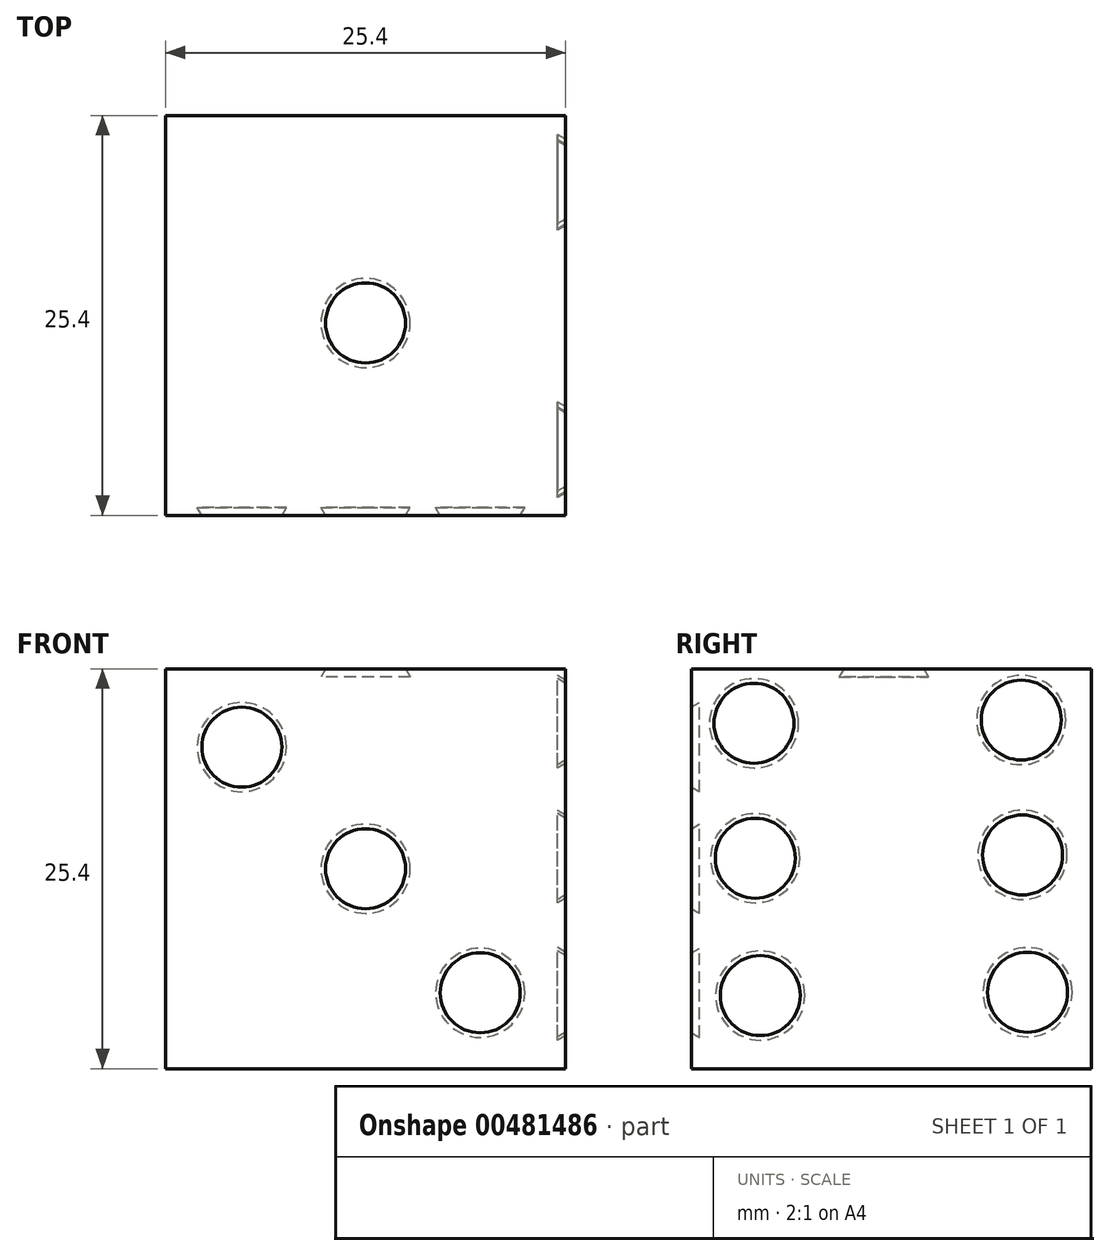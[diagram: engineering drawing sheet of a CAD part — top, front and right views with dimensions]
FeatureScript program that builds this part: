
annotation { "Feature Type Name" : "Feature", "Feature Type Description" : "" }
export const myFeature = defineFeature(function(context is Context, id is Id, definition is map)
    precondition{}
    {
        {
            var Q0;
            Q0=qCreatedBy(makeId("Front.planeOp"),FACE);
            var sketch = newSketch(context, id + "F0", { "sketchPlane" : qUnion([Q0])});
            skLineSegment(sketch, "E0.bottom", {"start": v(-12.7, 12.7) * mm, "end": v(12.7, 12.7) * mm});
            skLineSegment(sketch, "E0.top", {"start": v(-12.7, -12.7) * mm, "end": v(12.7, -12.7) * mm});
            skLineSegment(sketch, "E0.left", {"start": v(-12.7, 12.7) * mm, "end": v(-12.7, -12.7) * mm});
            skLineSegment(sketch, "E0.right", {"start": v(12.7, 12.7) * mm, "end": v(12.7, -12.7) * mm});
            skPoint(sketch, "E0.middle", {"position": v(0, 0) * mm});
            skSolve(sketch);
        }
        {
            var Q0;
            Q0=makeQuery(id+"F0.imprint","IMPRINT",FACE,{"disambiguationData":[TD([[makeQuery(id+"F0.imprint","IMPRINT",EDGE,{"derivedFrom":sQuery(id+"F0.wireOp",EDGE,"E0.bottom")}),-1.0]])]});
            extrude(context, id + "F1", {"entities" : qUnion([Q0]), "depth" : 25.4 * mm});
        }
        {
            var Q0;
            Q0=makeQuery(id+"F1.opExtrude","SWEPT_FACE",FACE,{"disambiguationData":[OSD([sQuery(id+"F0.wireOp",EDGE,"E0.bottom")])]});
            var sketch = newSketch(context, id + "F2", { "sketchPlane" : qUnion([Q0])});
            skCircle(sketch, "E1", {"center": v(0, -13.19) * mm, "radius": 2.54 * mm});
            skSolve(sketch);
        }
        {
            var Q0;
            Q0=makeQuery(id+"F2.imprint","IMPRINT",FACE,{"disambiguationData":[TD([[makeQuery(id+"F2.imprint","IMPRINT",EDGE,{"derivedFrom":sQuery(id+"F2.wireOp",EDGE,"E1")}),1.0]])]});
            extrude(context, id + "F3", {"entities" : qUnion([Q0]), "operationType" : NewBodyOperationType.REMOVE, "oppositeDirection" : true, "depth" : 0.5 * mm, "hasDraft" : true, "draftAngle" : 30 * degree});
        }
        {
            var Q0;
            Q0=makeQuery(id+"F1.opExtrude","CAP_FACE",FACE,{"disambiguationData":[OSD([sQuery(id+"F0.wireOp",EDGE,"E0.bottom"),sQuery(id+"F0.wireOp",EDGE,"E0.top"),sQuery(id+"F0.wireOp",EDGE,"E0.left"),sQuery(id+"F0.wireOp",EDGE,"E0.right")])],"isStart":false});
            var sketch = newSketch(context, id + "F4", { "sketchPlane" : qUnion([Q0])});
            skCircle(sketch, "E2", {"center": v(0, 0) * mm, "radius": 2.54 * mm});
            skCircle(sketch, "E3", {"center": v(7.28, -7.88) * mm, "radius": 2.54 * mm});
            skCircle(sketch, "E4", {"center": v(-7.86, 7.72) * mm, "radius": 2.54 * mm});
            skSolve(sketch);
        }
        {
            var Q0;
            Q0=makeQuery(id+"F4.imprint","IMPRINT",FACE,{"disambiguationData":[TD([[makeQuery(id+"F4.imprint","IMPRINT",EDGE,{"derivedFrom":sQuery(id+"F4.wireOp",EDGE,"E4")}),1.0]])]});
            var Q1;
            Q1=makeQuery(id+"F4.imprint","IMPRINT",FACE,{"disambiguationData":[TD([[makeQuery(id+"F4.imprint","IMPRINT",EDGE,{"derivedFrom":sQuery(id+"F4.wireOp",EDGE,"E2")}),1.0]])]});
            var Q2;
            Q2=makeQuery(id+"F4.imprint","IMPRINT",FACE,{"disambiguationData":[TD([[makeQuery(id+"F4.imprint","IMPRINT",EDGE,{"derivedFrom":sQuery(id+"F4.wireOp",EDGE,"E3")}),1.0]])]});
            extrude(context, id + "F5", {"entities" : qUnion([Q0, Q1, Q2]), "operationType" : NewBodyOperationType.REMOVE, "oppositeDirection" : true, "depth" : 0.5 * mm, "hasDraft" : true, "draftAngle" : 30 * degree});
        }
        {
            var Q0;
            Q0=makeQuery(id+"F1.opExtrude","SWEPT_FACE",FACE,{"disambiguationData":[OSD([sQuery(id+"F0.wireOp",EDGE,"E0.right")])]});
            var sketch = newSketch(context, id + "F6", { "sketchPlane" : qUnion([Q0])});
            skCircle(sketch, "E5", {"center": v(-21.43, 9.24) * mm, "radius": 2.54 * mm});
            skCircle(sketch, "E6", {"center": v(-21.35, 0.67) * mm, "radius": 2.54 * mm});
            skCircle(sketch, "E7", {"center": v(-21.03, -8.05) * mm, "radius": 2.54 * mm});
            skCircle(sketch, "E8", {"center": v(-4.45, 9.44) * mm, "radius": 2.54 * mm});
            skCircle(sketch, "E9", {"center": v(-4.38, 0.88) * mm, "radius": 2.54 * mm});
            skCircle(sketch, "E10", {"center": v(-4.05, -7.85) * mm, "radius": 2.54 * mm});
            skSolve(sketch);
        }
        {
            var Q0;
            Q0=makeQuery(id+"F6.imprint","IMPRINT",FACE,{"disambiguationData":[TD([[makeQuery(id+"F6.imprint","IMPRINT",EDGE,{"derivedFrom":sQuery(id+"F6.wireOp",EDGE,"E5")}),1.0]])]});
            var Q1;
            Q1=makeQuery(id+"F6.imprint","IMPRINT",FACE,{"disambiguationData":[TD([[makeQuery(id+"F6.imprint","IMPRINT",EDGE,{"derivedFrom":sQuery(id+"F6.wireOp",EDGE,"E6")}),1.0]])]});
            var Q2;
            Q2=makeQuery(id+"F6.imprint","IMPRINT",FACE,{"disambiguationData":[TD([[makeQuery(id+"F6.imprint","IMPRINT",EDGE,{"derivedFrom":sQuery(id+"F6.wireOp",EDGE,"E7")}),1.0]])]});
            var Q3;
            Q3=makeQuery(id+"F6.imprint","IMPRINT",FACE,{"disambiguationData":[TD([[makeQuery(id+"F6.imprint","IMPRINT",EDGE,{"derivedFrom":sQuery(id+"F6.wireOp",EDGE,"E8")}),1.0]])]});
            var Q4;
            Q4=makeQuery(id+"F6.imprint","IMPRINT",FACE,{"disambiguationData":[TD([[makeQuery(id+"F6.imprint","IMPRINT",EDGE,{"derivedFrom":sQuery(id+"F6.wireOp",EDGE,"E9")}),1.0]])]});
            var Q5;
            Q5=makeQuery(id+"F6.imprint","IMPRINT",FACE,{"disambiguationData":[TD([[makeQuery(id+"F6.imprint","IMPRINT",EDGE,{"derivedFrom":sQuery(id+"F6.wireOp",EDGE,"E10")}),1.0]])]});
            extrude(context, id + "F7", {"entities" : qUnion([Q0, Q1, Q2, Q3, Q4, Q5]), "operationType" : NewBodyOperationType.REMOVE, "oppositeDirection" : true, "depth" : 0.5 * mm, "hasDraft" : true, "draftAngle" : 30 * degree});
        }
    });
